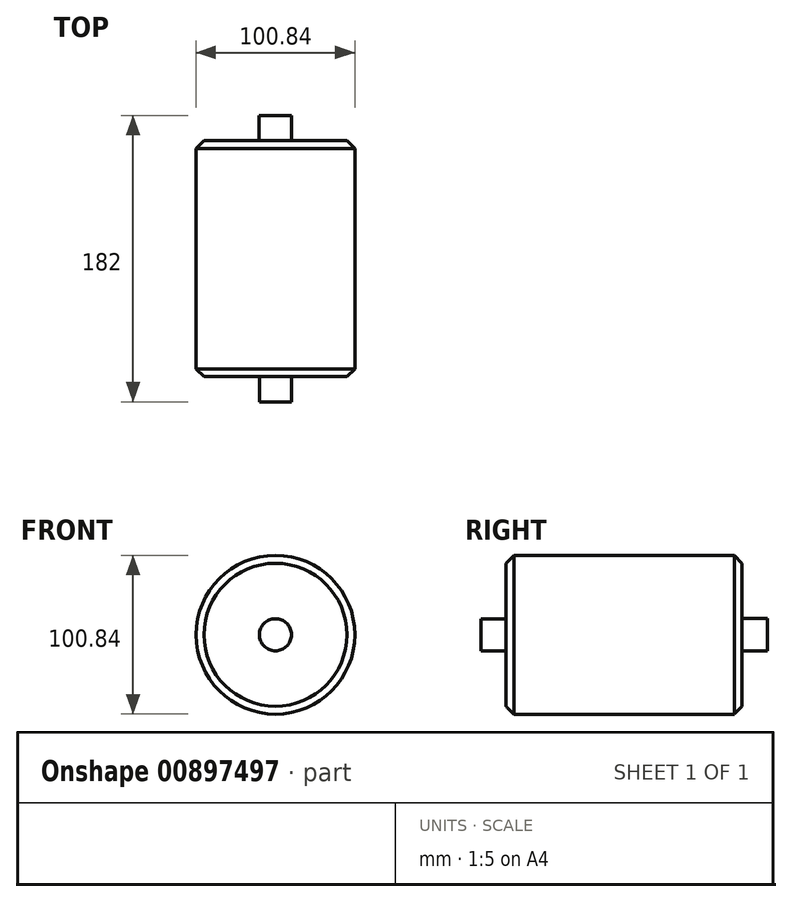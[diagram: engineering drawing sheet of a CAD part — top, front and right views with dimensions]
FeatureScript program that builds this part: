
annotation { "Feature Type Name" : "Feature", "Feature Type Description" : "" }
export const myFeature = defineFeature(function(context is Context, id is Id, definition is map)
    precondition{}
    {
        {
            var Q0;
            Q0=qCreatedBy(makeId("Front.planeOp"),FACE);
            var sketch = newSketch(context, id + "F0", { "sketchPlane" : qUnion([Q0])});
            skCircle(sketch, "E0", {"center": v(0, 0) * mm, "radius": 50.42 * mm});
            skSolve(sketch);
        }
        {
            var Q0;
            Q0=makeQuery(id+"F0.imprint","IMPRINT",FACE,{"disambiguationData":[TD([[makeQuery(id+"F0.imprint","IMPRINT",EDGE,{"derivedFrom":sQuery(id+"F0.wireOp",EDGE,"E0")}),1.0]])]});
            extrude(context, id + "F1", {"entities" : qUnion([Q0]), "depth" : 150 * mm, "offsetDistance" : 25.4 * mm});
        }
        {
            var Q0;
            Q0=makeQuery(id+"F1.opExtrude","CAP_FACE",FACE,{"disambiguationData":[OSD([sQuery(id+"F0.wireOp",EDGE,"E0")])],"isStart":false});
            chamfer(context, id + "F2", {"entities" : qUnion([Q0]), "width" : 5 * mm, "tangentPropagation" : true});
        }
        {
            var Q0;
            Q0=makeQuery(id+"F1.opExtrude","CAP_FACE",FACE,{"disambiguationData":[OSD([sQuery(id+"F0.wireOp",EDGE,"E0")])],"isStart":false});
            var sketch = newSketch(context, id + "F3", { "sketchPlane" : qUnion([Q0])});
            skCircle(sketch, "E1", {"center": v(0, 0) * mm, "radius": 10.18 * mm});
            skSolve(sketch);
        }
        {
            var Q0;
            Q0=makeQuery(id+"F3.imprint","IMPRINT",FACE,{"disambiguationData":[TD([[makeQuery(id+"F3.imprint","IMPRINT",EDGE,{"derivedFrom":sQuery(id+"F3.wireOp",EDGE,"E1")}),1.0]])]});
            extrude(context, id + "F4", {"entities" : qUnion([Q0]), "operationType" : NewBodyOperationType.ADD, "depth" : 16 * mm, "offsetDistance" : 25.4 * mm});
        }
        {
            var Q0;
            Q0=makeQuery(id+"F1.opExtrude","CAP_FACE",FACE,{"disambiguationData":[OSD([sQuery(id+"F0.wireOp",EDGE,"E0")])],"isStart":true});
            chamfer(context, id + "F5", {"entities" : qUnion([Q0]), "width" : 5 * mm, "tangentPropagation" : true});
        }
        {
            var Q0;
            Q0=makeQuery(id+"F1.opExtrude","CAP_FACE",FACE,{"disambiguationData":[OSD([sQuery(id+"F0.wireOp",EDGE,"E0")])],"isStart":true});
            var sketch = newSketch(context, id + "F6", { "sketchPlane" : qUnion([Q0])});
            skCircle(sketch, "E2", {"center": v(0, 0) * mm, "radius": 10.34 * mm});
            skSolve(sketch);
        }
        {
            var Q0;
            Q0=makeQuery(id+"F6.imprint","IMPRINT",FACE,{"disambiguationData":[TD([[makeQuery(id+"F6.imprint","IMPRINT",EDGE,{"derivedFrom":sQuery(id+"F6.wireOp",EDGE,"E2")}),1.0]])]});
            extrude(context, id + "F7", {"entities" : qUnion([Q0]), "operationType" : NewBodyOperationType.ADD, "depth" : 16 * mm, "offsetDistance" : 25.4 * mm});
        }
    });
